# Revit family: Atdec-Wall_Mount-ADB_VWP-
name_source: partatom
category: Generic Models
revit_build: Autodesk Revit 2016 (Build: 20150220_1215(x64)
units: mm (PartAtom-declared; Revit-internal decimal feet)

## family parameters
Can host rebar = No
Cut with Voids When Loaded = No
Host = Face
Part Type = Normal
Room Calculation Point = No
Round Connector Dimension = Use Diameter
Shared = No

## types (1)
- ADB-VWP
    Assembly Code = E1010800
    Bracket Distance = 440 mm
    Colour Options = Black
    Default Elevation = 1219 mm
    Description = pop-out video wall mount
    Flat screen maximum supported weight = 50kg (110lb)
    Manufacturer = Atdec
    Master Carton Dimensions = 660mm (26") Lenght, 600mm (23.6") Width, 110mm (4.3") Height
    Material = Steel
    Maximum distance from wall (mm) = 267mm (10.5")
    Minimum distance from wall (mm) = 88mm (3.46")
    Model = ADB-VWP
    Pan Adjustment = -
    Product Family = Wall Mount Rail
    Product information link = https://www.atdec.com.au
    Range of Motion = Fixed Angle
    Security feature = Can be secured with padlock (not included)
    Single Unit Dimensions = 650mm (25.5") Lenght, 587mm (23.1") Width, 100mm (3.9") Height
    Single units per master pack = 1
    Tilt Adjustment = -
    UPC Code = 881493016231
    URL = www.atdec.com.au
    Universal Height (mm) = From 100 to 400
    Universal Width (mm) = From 100 to 600
    VESA mounting hole pattern, mm = 100x100, 100x200, 200x100, 200x200, 200x300, 200x400, 200x600, 300x200, 300x300, 400x200, 400x300, 400x400, 400x600, 600x200, 600x400
    Warranty = 10 years
    Weight, master carton = 15.5kg (34lb)
    Weight, single unit = 5.92kg (13lb)

## geometry (parser evidence)
native form markers: Sweep x5
no freeform markers — native parametric forms only
